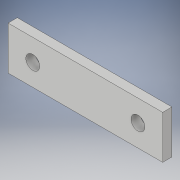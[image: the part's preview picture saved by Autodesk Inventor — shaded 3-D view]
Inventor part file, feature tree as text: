
AUTODESK INVENTOR PART (.ipt)
format: ipt  version: 2017 (Build 210142000, 142)  size: 104,448 bytes
history: native  units: in
note: dims shown in document units (in); Inventor stores cm internally (conversion verified against a paired STEP export)
features: sketch x7, extrude x1, hole x1
ambient origin geometry x8: Origin, YZ Plane, XZ Plane, XY Plane, X Axis, Y Axis, Z Axis, Center Point
bodies: Solid1 (feature_tree)
feature tree (9):
  extrude  "Extrusion1"  Depth=0.5512in
  hole  "Hole1"  [1 undecoded]
  sketch  "Sketch3"  dims[d5=0.2756in]
  sketch  "Sketch4"  dims[d6=1.3386in]
  sketch  "Sketch5"  dims[d7=0.1772in d8=0.2362in d9=0.1575in d10=0.0787in d11=90.0deg d12=0.315in d13=0.8108in]
  sketch  "Sketch6"  dims[d14=0.315in]
  sketch  "Sketch7"
  sketch  "Sketch1"  dims[d0=1.9685in d1=0.5512in]
  sketch  "Sketch2"  dims[d2=0.1181in d3=0.0in d4=0.2756in]
note: 1 required parameter value undecoded (feature->parameter linkage not recoverable at this tier; creation-order binding heuristic only, values carry confidence <= 0.55)
